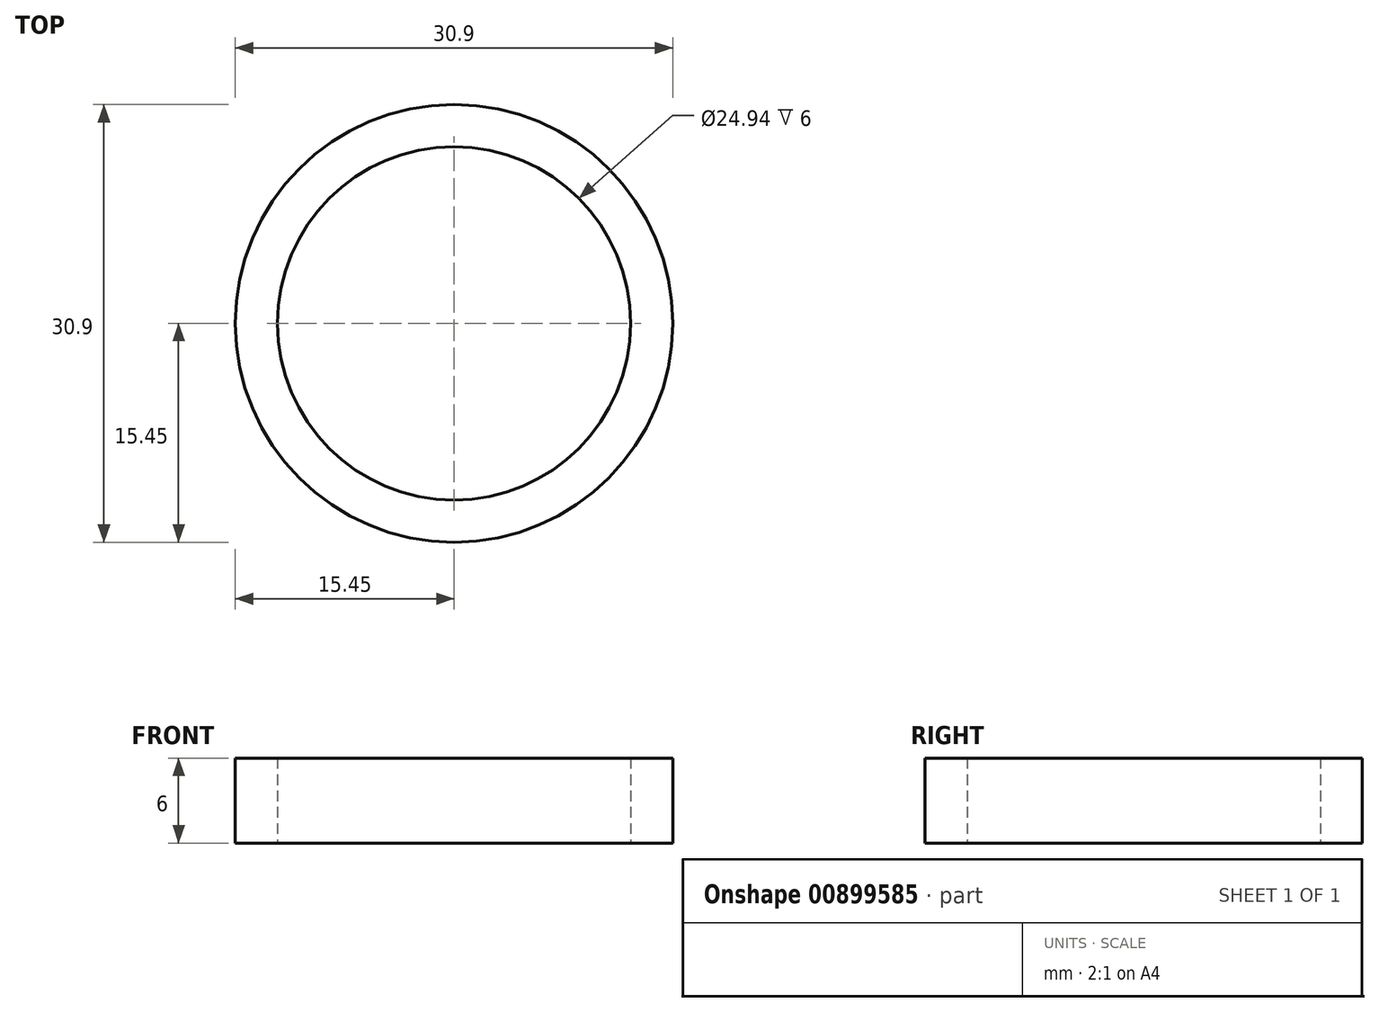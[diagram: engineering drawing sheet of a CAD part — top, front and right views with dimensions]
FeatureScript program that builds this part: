
annotation { "Feature Type Name" : "Feature", "Feature Type Description" : "" }
export const myFeature = defineFeature(function(context is Context, id is Id, definition is map)
    precondition{}
    {
        {
            var Q0;
            Q0=qCreatedBy(makeId("Top.planeOp"),FACE);
            var sketch = newSketch(context, id + "F0", { "sketchPlane" : qUnion([Q0])});
            skCircle(sketch, "E0", {"center": v(0, 0) * mm, "radius": 15.45 * mm});
            skCircle(sketch, "E1", {"center": v(0, 0) * mm, "radius": 12.47 * mm});
            skSolve(sketch);
        }
        {
            var Q0;
            Q0=makeQuery(id+"F0.imprint","IMPRINT",FACE,{"disambiguationData":[TD([[makeQuery(id+"F0.imprint","IMPRINT",EDGE,{"derivedFrom":sQuery(id+"F0.wireOp",EDGE,"E0")}),1.0]])]});
            extrude(context, id + "F1", {"entities" : qUnion([Q0]), "depth" : 6 * mm, "offsetDistance" : 25 * mm});
        }
    });
